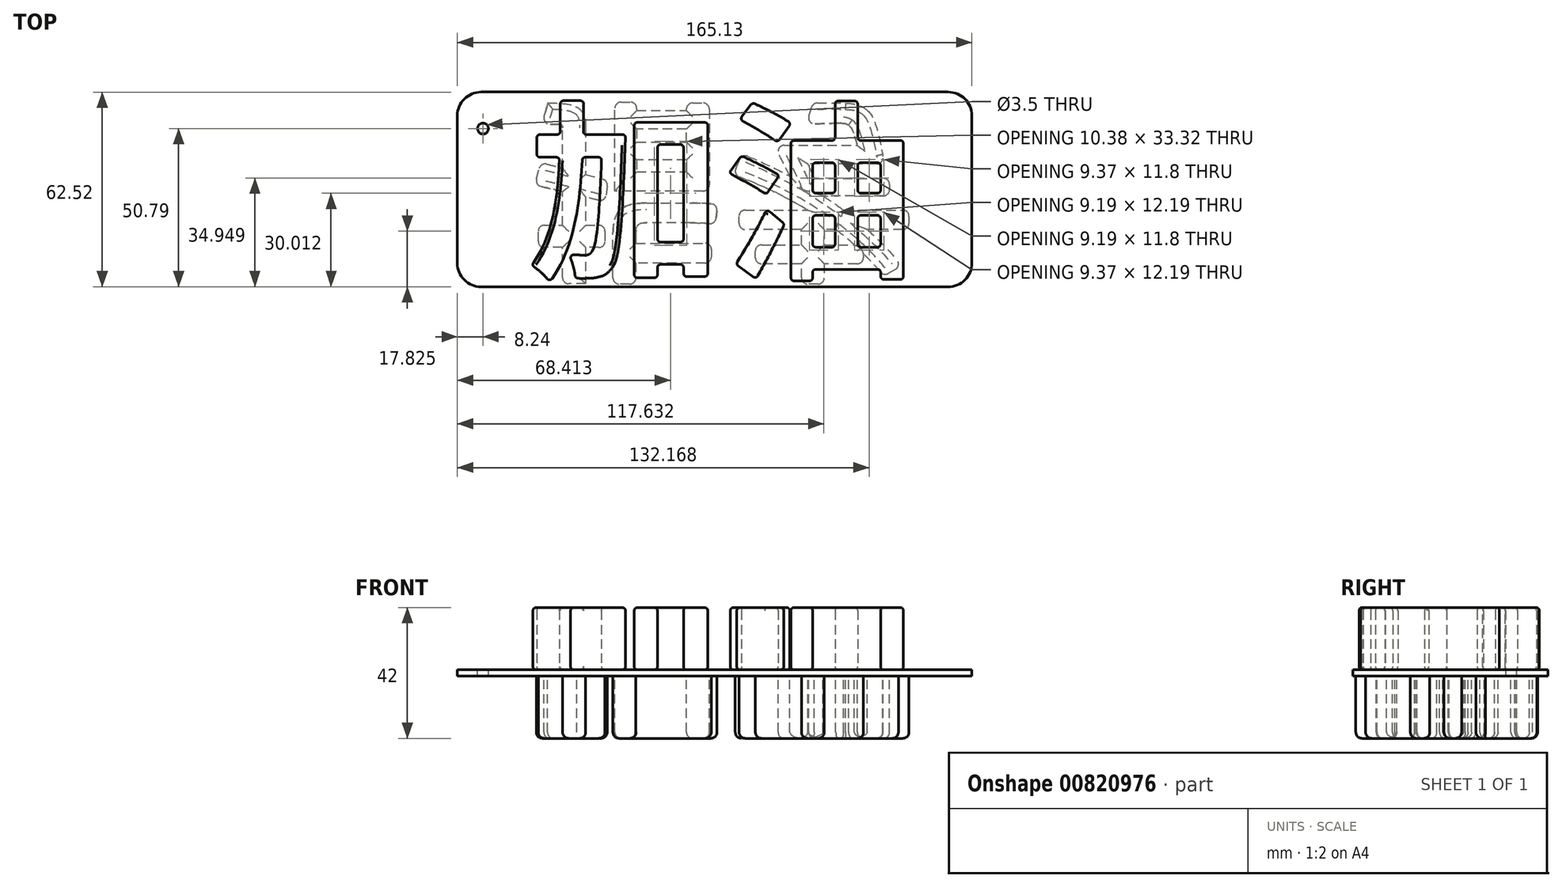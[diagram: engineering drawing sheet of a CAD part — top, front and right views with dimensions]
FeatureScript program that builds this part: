
annotation { "Feature Type Name" : "Feature", "Feature Type Description" : "" }
export const myFeature = defineFeature(function(context is Context, id is Id, definition is map)
    precondition{}
    {
        {
            var Q0;
            Q0=qCreatedBy(makeId("Top.planeOp"),FACE);
            var sketch = newSketch(context, id + "F0", { "sketchPlane" : qUnion([Q0])});
            skText(sketch, "E0", { "text": "加油", "fontName": "NotoSansCJKtc-Bold.otf"});
            const initialGuessF0  = {"E0": [-0.06597, -0.02194, 1, 0, 0.045]};
            skSetInitialGuess(sketch, initialGuessF0);
            skSolve(sketch);
        }
        {
            var Q0;
            Q0 = qSketchRegion(id + "F0", true);
            extrude(context, id + "F1", {"entities" : qUnion([Q0]), "depth" : 20 * mm, "offsetDistance" : 25.4 * mm});
        }
        {
            var Q0;
            Q0=makeQuery(id+"F1.opExtrude","CAP_EDGE",EDGE,{"disambiguationData":[OSD([sQuery(id+"F0.wireOp",EDGE,"E0.sketch_text.stroke-3")])],"isStart":false});
            var Q1;
            Q1=makeQuery(id+"F1.opExtrude","CAP_EDGE",EDGE,{"disambiguationData":[OSD([sQuery(id+"F0.wireOp",EDGE,"E0.sketch_text.stroke-35")])],"isStart":false});
            var Q2;
            Q2=makeQuery(id+"F1.opExtrude","CAP_EDGE",EDGE,{"disambiguationData":[OSD([sQuery(id+"F0.wireOp",EDGE,"E0.sketch_text.stroke-36")])],"isStart":false});
            var Q3;
            Q3=makeQuery(id+"F1.opExtrude","CAP_EDGE",EDGE,{"disambiguationData":[OSD([sQuery(id+"F0.wireOp",EDGE,"E0.sketch_text.stroke-37")])],"isStart":true});
            var Q4;
            Q4=makeQuery(id+"F1.opExtrude","CAP_EDGE",EDGE,{"disambiguationData":[OSD([sQuery(id+"F0.wireOp",EDGE,"E0.sketch_text.stroke-37")])],"isStart":false});
            var Q5;
            Q5=makeQuery(id+"F1.opExtrude","SWEPT_EDGE",EDGE,{"disambiguationData":[OSD([sQuery(id+"F0.wireOp",EDGE,"E0.sketch_text.stroke-31"),sQuery(id+"F0.wireOp",EDGE,"E0.sketch_text.stroke-34")])]});
            var Q6;
            Q6=makeQuery(id+"F1.opExtrude","CAP_EDGE",EDGE,{"disambiguationData":[OSD([sQuery(id+"F0.wireOp",EDGE,"E0.sketch_text.stroke-33")])],"isStart":false});
            var Q7;
            Q7=makeQuery(id+"F1.opExtrude","CAP_EDGE",EDGE,{"disambiguationData":[OSD([sQuery(id+"F0.wireOp",EDGE,"E0.sketch_text.stroke-34")])],"isStart":true});
            var Q8;
            Q8=makeQuery(id+"F1.opExtrude","CAP_EDGE",EDGE,{"disambiguationData":[OSD([sQuery(id+"F0.wireOp",EDGE,"E0.sketch_text.stroke-34")])],"isStart":false});
            var Q9;
            Q9=makeQuery(id+"F1.opExtrude","CAP_EDGE",EDGE,{"disambiguationData":[OSD([sQuery(id+"F0.wireOp",EDGE,"E0.sketch_text.stroke-39")])],"isStart":true});
            var Q10;
            Q10=makeQuery(id+"F1.opExtrude","CAP_EDGE",EDGE,{"disambiguationData":[OSD([sQuery(id+"F0.wireOp",EDGE,"E0.sketch_text.stroke-39")])],"isStart":false});
            var Q11;
            Q11=makeQuery(id+"F1.opExtrude","CAP_EDGE",EDGE,{"disambiguationData":[OSD([sQuery(id+"F0.wireOp",EDGE,"E0.sketch_text.stroke-40")])],"isStart":false});
            var Q12;
            Q12=makeQuery(id+"F1.opExtrude","CAP_EDGE",EDGE,{"disambiguationData":[OSD([sQuery(id+"F0.wireOp",EDGE,"E0.sketch_text.stroke-41")])],"isStart":false});
            var Q13;
            Q13=makeQuery(id+"F1.opExtrude","CAP_EDGE",EDGE,{"disambiguationData":[OSD([sQuery(id+"F0.wireOp",EDGE,"E0.sketch_text.stroke-42")])],"isStart":true});
            var Q14;
            Q14=makeQuery(id+"F1.opExtrude","CAP_EDGE",EDGE,{"disambiguationData":[OSD([sQuery(id+"F0.wireOp",EDGE,"E0.sketch_text.stroke-42")])],"isStart":false});
            var Q15;
            Q15=makeQuery(id+"F1.opExtrude","SWEPT_EDGE",EDGE,{"disambiguationData":[OSD([sQuery(id+"F0.wireOp",EDGE,"E0.sketch_text.stroke-0"),sQuery(id+"F0.wireOp",EDGE,"E0.sketch_text.stroke-18")])]});
            var Q16;
            Q16=makeQuery(id+"F1.opExtrude","SWEPT_EDGE",EDGE,{"disambiguationData":[OSD([sQuery(id+"F0.wireOp",EDGE,"E0.sketch_text.stroke-2"),sQuery(id+"F0.wireOp",EDGE,"E0.sketch_text.stroke-3")])]});
            var Q17;
            Q17=makeQuery(id+"F1.opExtrude","SWEPT_EDGE",EDGE,{"disambiguationData":[OSD([sQuery(id+"F0.wireOp",EDGE,"E0.sketch_text.stroke-4"),sQuery(id+"F0.wireOp",EDGE,"E0.sketch_text.stroke-5")])]});
            var Q18;
            Q18=makeQuery(id+"F1.opExtrude","CAP_EDGE",EDGE,{"disambiguationData":[OSD([sQuery(id+"F0.wireOp",EDGE,"E0.sketch_text.stroke-11")])],"isStart":false});
            var Q19;
            Q19=makeQuery(id+"F1.opExtrude","CAP_EDGE",EDGE,{"disambiguationData":[OSD([sQuery(id+"F0.wireOp",EDGE,"E0.sketch_text.stroke-12")])],"isStart":false});
            var Q20;
            Q20=makeQuery(id+"F1.opExtrude","CAP_EDGE",EDGE,{"disambiguationData":[OSD([sQuery(id+"F0.wireOp",EDGE,"E0.sketch_text.stroke-13")])],"isStart":true});
            var Q21;
            Q21=makeQuery(id+"F1.opExtrude","CAP_EDGE",EDGE,{"disambiguationData":[OSD([sQuery(id+"F0.wireOp",EDGE,"E0.sketch_text.stroke-13")])],"isStart":false});
            var Q22;
            Q22=makeQuery(id+"F1.opExtrude","CAP_EDGE",EDGE,{"disambiguationData":[OSD([sQuery(id+"F0.wireOp",EDGE,"E0.sketch_text.stroke-6")])],"isStart":true});
            var Q23;
            Q23=makeQuery(id+"F1.opExtrude","CAP_EDGE",EDGE,{"disambiguationData":[OSD([sQuery(id+"F0.wireOp",EDGE,"E0.sketch_text.stroke-14")])],"isStart":true});
            var Q24;
            Q24=makeQuery(id+"F1.opExtrude","CAP_EDGE",EDGE,{"disambiguationData":[OSD([sQuery(id+"F0.wireOp",EDGE,"E0.sketch_text.stroke-6")])],"isStart":false});
            var Q25;
            Q25=makeQuery(id+"F1.opExtrude","CAP_EDGE",EDGE,{"disambiguationData":[OSD([sQuery(id+"F0.wireOp",EDGE,"E0.sketch_text.stroke-14")])],"isStart":false});
            var Q26;
            Q26=makeQuery(id+"F1.opExtrude","CAP_EDGE",EDGE,{"disambiguationData":[OSD([sQuery(id+"F0.wireOp",EDGE,"E0.sketch_text.stroke-7")])],"isStart":true});
            var Q27;
            Q27=makeQuery(id+"F1.opExtrude","CAP_EDGE",EDGE,{"disambiguationData":[OSD([sQuery(id+"F0.wireOp",EDGE,"E0.sketch_text.stroke-15")])],"isStart":true});
            var Q28;
            Q28=makeQuery(id+"F1.opExtrude","CAP_EDGE",EDGE,{"disambiguationData":[OSD([sQuery(id+"F0.wireOp",EDGE,"E0.sketch_text.stroke-7")])],"isStart":false});
            var Q29;
            Q29=makeQuery(id+"F1.opExtrude","CAP_EDGE",EDGE,{"disambiguationData":[OSD([sQuery(id+"F0.wireOp",EDGE,"E0.sketch_text.stroke-15")])],"isStart":false});
            var Q30;
            Q30=makeQuery(id+"F1.opExtrude","CAP_EDGE",EDGE,{"disambiguationData":[OSD([sQuery(id+"F0.wireOp",EDGE,"E0.sketch_text.stroke-8")])],"isStart":true});
            var Q31;
            Q31=makeQuery(id+"F1.opExtrude","CAP_EDGE",EDGE,{"disambiguationData":[OSD([sQuery(id+"F0.wireOp",EDGE,"E0.sketch_text.stroke-16")])],"isStart":true});
            var Q32;
            Q32=makeQuery(id+"F1.opExtrude","CAP_EDGE",EDGE,{"disambiguationData":[OSD([sQuery(id+"F0.wireOp",EDGE,"E0.sketch_text.stroke-8")])],"isStart":false});
            var Q33;
            Q33=makeQuery(id+"F1.opExtrude","CAP_EDGE",EDGE,{"disambiguationData":[OSD([sQuery(id+"F0.wireOp",EDGE,"E0.sketch_text.stroke-16")])],"isStart":false});
            var Q34;
            Q34=makeQuery(id+"F1.opExtrude","CAP_EDGE",EDGE,{"disambiguationData":[OSD([sQuery(id+"F0.wireOp",EDGE,"E0.sketch_text.stroke-17")])],"isStart":false});
            var Q35;
            Q35=makeQuery(id+"F1.opExtrude","CAP_EDGE",EDGE,{"disambiguationData":[OSD([sQuery(id+"F0.wireOp",EDGE,"E0.sketch_text.stroke-10")])],"isStart":false});
            var Q36;
            Q36=makeQuery(id+"F1.opExtrude","SWEPT_EDGE",EDGE,{"disambiguationData":[OSD([sQuery(id+"F0.wireOp",EDGE,"E0.sketch_text.stroke-28"),sQuery(id+"F0.wireOp",EDGE,"E0.sketch_text.stroke-29")])]});
            var Q37;
            Q37=makeQuery(id+"F1.opExtrude","SWEPT_EDGE",EDGE,{"disambiguationData":[OSD([sQuery(id+"F0.wireOp",EDGE,"E0.sketch_text.stroke-23"),sQuery(id+"F0.wireOp",EDGE,"E0.sketch_text.stroke-24")])]});
            var Q38;
            Q38=makeQuery(id+"F1.opExtrude","SWEPT_EDGE",EDGE,{"disambiguationData":[OSD([sQuery(id+"F0.wireOp",EDGE,"E0.sketch_text.stroke-24"),sQuery(id+"F0.wireOp",EDGE,"E0.sketch_text.stroke-25")])]});
            var Q39;
            Q39=makeQuery(id+"F1.opExtrude","SWEPT_EDGE",EDGE,{"disambiguationData":[OSD([sQuery(id+"F0.wireOp",EDGE,"E0.sketch_text.stroke-27"),sQuery(id+"F0.wireOp",EDGE,"E0.sketch_text.stroke-28")])]});
            var Q40;
            Q40=makeQuery(id+"F1.opExtrude","SWEPT_EDGE",EDGE,{"disambiguationData":[OSD([sQuery(id+"F0.wireOp",EDGE,"E0.sketch_text.stroke-45"),sQuery(id+"F0.wireOp",EDGE,"E0.sketch_text.stroke-46")])]});
            var Q41;
            Q41=makeQuery(id+"F1.opExtrude","SWEPT_EDGE",EDGE,{"disambiguationData":[OSD([sQuery(id+"F0.wireOp",EDGE,"E0.sketch_text.stroke-61"),sQuery(id+"F0.wireOp",EDGE,"E0.sketch_text.stroke-62")])]});
            var Q42;
            Q42=makeQuery(id+"F1.opExtrude","SWEPT_EDGE",EDGE,{"disambiguationData":[OSD([sQuery(id+"F0.wireOp",EDGE,"E0.sketch_text.stroke-63"),sQuery(id+"F0.wireOp",EDGE,"E0.sketch_text.stroke-64")])]});
            var Q43;
            Q43=makeQuery(id+"F1.opExtrude","SWEPT_EDGE",EDGE,{"disambiguationData":[OSD([sQuery(id+"F0.wireOp",EDGE,"E0.sketch_text.stroke-48"),sQuery(id+"F0.wireOp",EDGE,"E0.sketch_text.stroke-49")])]});
            var Q44;
            Q44=makeQuery(id+"F1.opExtrude","SWEPT_EDGE",EDGE,{"disambiguationData":[OSD([sQuery(id+"F0.wireOp",EDGE,"E0.sketch_text.stroke-64"),sQuery(id+"F0.wireOp",EDGE,"E0.sketch_text.stroke-65")])]});
            var Q45;
            Q45=makeQuery(id+"F1.opExtrude","SWEPT_EDGE",EDGE,{"disambiguationData":[OSD([sQuery(id+"F0.wireOp",EDGE,"E0.sketch_text.stroke-49"),sQuery(id+"F0.wireOp",EDGE,"E0.sketch_text.stroke-50")])]});
            var Q46;
            Q46=makeQuery(id+"F1.opExtrude","SWEPT_EDGE",EDGE,{"disambiguationData":[OSD([sQuery(id+"F0.wireOp",EDGE,"E0.sketch_text.stroke-51"),sQuery(id+"F0.wireOp",EDGE,"E0.sketch_text.stroke-52")])]});
            var Q47;
            Q47=makeQuery(id+"F1.opExtrude","SWEPT_EDGE",EDGE,{"disambiguationData":[OSD([sQuery(id+"F0.wireOp",EDGE,"E0.sketch_text.stroke-67"),sQuery(id+"F0.wireOp",EDGE,"E0.sketch_text.stroke-68")])]});
            var Q48;
            Q48=makeQuery(id+"F1.opExtrude","SWEPT_EDGE",EDGE,{"disambiguationData":[OSD([sQuery(id+"F0.wireOp",EDGE,"E0.sketch_text.stroke-52"),sQuery(id+"F0.wireOp",EDGE,"E0.sketch_text.stroke-53")])]});
            var Q49;
            Q49=makeQuery(id+"F1.opExtrude","SWEPT_EDGE",EDGE,{"disambiguationData":[OSD([sQuery(id+"F0.wireOp",EDGE,"E0.sketch_text.stroke-68"),sQuery(id+"F0.wireOp",EDGE,"E0.sketch_text.stroke-69")])]});
            var Q50;
            Q50=makeQuery(id+"F1.opExtrude","SWEPT_EDGE",EDGE,{"disambiguationData":[OSD([sQuery(id+"F0.wireOp",EDGE,"E0.sketch_text.stroke-55"),sQuery(id+"F0.wireOp",EDGE,"E0.sketch_text.stroke-56")])]});
            var Q51;
            Q51=makeQuery(id+"F1.opExtrude","SWEPT_EDGE",EDGE,{"disambiguationData":[OSD([sQuery(id+"F0.wireOp",EDGE,"E0.sketch_text.stroke-56"),sQuery(id+"F0.wireOp",EDGE,"E0.sketch_text.stroke-57")])]});
            var Q52;
            Q52=makeQuery(id+"F1.opExtrude","SWEPT_EDGE",EDGE,{"disambiguationData":[OSD([sQuery(id+"F0.wireOp",EDGE,"E0.sketch_text.stroke-43"),sQuery(id+"F0.wireOp",EDGE,"E0.sketch_text.stroke-46")])]});
            var Q53;
            Q53=makeQuery(id+"F1.opExtrude","SWEPT_EDGE",EDGE,{"disambiguationData":[OSD([sQuery(id+"F0.wireOp",EDGE,"E0.sketch_text.stroke-59"),sQuery(id+"F0.wireOp",EDGE,"E0.sketch_text.stroke-70")])]});
            var Q54;
            Q54=makeQuery(id+"F1.opExtrude","CAP_EDGE",EDGE,{"disambiguationData":[OSD([sQuery(id+"F0.wireOp",EDGE,"E0.sketch_text.stroke-35")])],"isStart":true});
            var Q55;
            Q55=makeQuery(id+"F1.opExtrude","CAP_EDGE",EDGE,{"disambiguationData":[OSD([sQuery(id+"F0.wireOp",EDGE,"E0.sketch_text.stroke-36")])],"isStart":true});
            var Q56;
            Q56=makeQuery(id+"F1.opExtrude","SWEPT_EDGE",EDGE,{"disambiguationData":[OSD([sQuery(id+"F0.wireOp",EDGE,"E0.sketch_text.stroke-35"),sQuery(id+"F0.wireOp",EDGE,"E0.sketch_text.stroke-38")])]});
            var Q57;
            Q57=makeQuery(id+"F1.opExtrude","SWEPT_EDGE",EDGE,{"disambiguationData":[OSD([sQuery(id+"F0.wireOp",EDGE,"E0.sketch_text.stroke-35"),sQuery(id+"F0.wireOp",EDGE,"E0.sketch_text.stroke-36")])]});
            var Q58;
            Q58=makeQuery(id+"F1.opExtrude","CAP_EDGE",EDGE,{"disambiguationData":[OSD([sQuery(id+"F0.wireOp",EDGE,"E0.sketch_text.stroke-38")])],"isStart":false});
            var Q59;
            Q59=makeQuery(id+"F1.opExtrude","SWEPT_EDGE",EDGE,{"disambiguationData":[OSD([sQuery(id+"F0.wireOp",EDGE,"E0.sketch_text.stroke-36"),sQuery(id+"F0.wireOp",EDGE,"E0.sketch_text.stroke-37")])]});
            var Q60;
            Q60=makeQuery(id+"F1.opExtrude","SWEPT_EDGE",EDGE,{"disambiguationData":[OSD([sQuery(id+"F0.wireOp",EDGE,"E0.sketch_text.stroke-37"),sQuery(id+"F0.wireOp",EDGE,"E0.sketch_text.stroke-38")])]});
            var Q61;
            Q61=makeQuery(id+"F1.opExtrude","SWEPT_EDGE",EDGE,{"disambiguationData":[OSD([sQuery(id+"F0.wireOp",EDGE,"E0.sketch_text.stroke-32"),sQuery(id+"F0.wireOp",EDGE,"E0.sketch_text.stroke-33")])]});
            var Q62;
            Q62=makeQuery(id+"F1.opExtrude","SWEPT_EDGE",EDGE,{"disambiguationData":[OSD([sQuery(id+"F0.wireOp",EDGE,"E0.sketch_text.stroke-33"),sQuery(id+"F0.wireOp",EDGE,"E0.sketch_text.stroke-34")])]});
            var Q63;
            Q63=makeQuery(id+"F1.opExtrude","CAP_EDGE",EDGE,{"disambiguationData":[OSD([sQuery(id+"F0.wireOp",EDGE,"E0.sketch_text.stroke-31")])],"isStart":true});
            var Q64;
            Q64=makeQuery(id+"F1.opExtrude","CAP_EDGE",EDGE,{"disambiguationData":[OSD([sQuery(id+"F0.wireOp",EDGE,"E0.sketch_text.stroke-32")])],"isStart":true});
            var Q65;
            Q65=makeQuery(id+"F1.opExtrude","CAP_EDGE",EDGE,{"disambiguationData":[OSD([sQuery(id+"F0.wireOp",EDGE,"E0.sketch_text.stroke-33")])],"isStart":true});
            var Q66;
            Q66=makeQuery(id+"F1.opExtrude","SWEPT_EDGE",EDGE,{"disambiguationData":[OSD([sQuery(id+"F0.wireOp",EDGE,"E0.sketch_text.stroke-39"),sQuery(id+"F0.wireOp",EDGE,"E0.sketch_text.stroke-42")])]});
            var Q67;
            Q67=makeQuery(id+"F1.opExtrude","CAP_EDGE",EDGE,{"disambiguationData":[OSD([sQuery(id+"F0.wireOp",EDGE,"E0.sketch_text.stroke-40")])],"isStart":true});
            var Q68;
            Q68=makeQuery(id+"F1.opExtrude","SWEPT_EDGE",EDGE,{"disambiguationData":[OSD([sQuery(id+"F0.wireOp",EDGE,"E0.sketch_text.stroke-39"),sQuery(id+"F0.wireOp",EDGE,"E0.sketch_text.stroke-40")])]});
            var Q69;
            Q69=makeQuery(id+"F1.opExtrude","SWEPT_EDGE",EDGE,{"disambiguationData":[OSD([sQuery(id+"F0.wireOp",EDGE,"E0.sketch_text.stroke-40"),sQuery(id+"F0.wireOp",EDGE,"E0.sketch_text.stroke-41")])]});
            var Q70;
            Q70=makeQuery(id+"F1.opExtrude","CAP_EDGE",EDGE,{"disambiguationData":[OSD([sQuery(id+"F0.wireOp",EDGE,"E0.sketch_text.stroke-41")])],"isStart":true});
            var Q71;
            Q71=makeQuery(id+"F1.opExtrude","SWEPT_EDGE",EDGE,{"disambiguationData":[OSD([sQuery(id+"F0.wireOp",EDGE,"E0.sketch_text.stroke-41"),sQuery(id+"F0.wireOp",EDGE,"E0.sketch_text.stroke-42")])]});
            var Q72;
            Q72=makeQuery(id+"F1.opExtrude","SWEPT_EDGE",EDGE,{"disambiguationData":[OSD([sQuery(id+"F0.wireOp",EDGE,"E0.sketch_text.stroke-12"),sQuery(id+"F0.wireOp",EDGE,"E0.sketch_text.stroke-13")])]});
            var Q73;
            Q73=makeQuery(id+"F1.opExtrude","SWEPT_EDGE",EDGE,{"disambiguationData":[OSD([sQuery(id+"F0.wireOp",EDGE,"E0.sketch_text.stroke-13"),sQuery(id+"F0.wireOp",EDGE,"E0.sketch_text.stroke-14")])]});
            var Q74;
            Q74=makeQuery(id+"F1.opExtrude","SWEPT_EDGE",EDGE,{"disambiguationData":[OSD([sQuery(id+"F0.wireOp",EDGE,"E0.sketch_text.stroke-14"),sQuery(id+"F0.wireOp",EDGE,"E0.sketch_text.stroke-15")])]});
            var Q75;
            Q75=makeQuery(id+"F1.opExtrude","SWEPT_EDGE",EDGE,{"disambiguationData":[OSD([sQuery(id+"F0.wireOp",EDGE,"E0.sketch_text.stroke-3"),sQuery(id+"F0.wireOp",EDGE,"E0.sketch_text.stroke-4")])]});
            var Q76;
            Q76=makeQuery(id+"F1.opExtrude","SWEPT_EDGE",EDGE,{"disambiguationData":[OSD([sQuery(id+"F0.wireOp",EDGE,"E0.sketch_text.stroke-5"),sQuery(id+"F0.wireOp",EDGE,"E0.sketch_text.stroke-6")])]});
            var Q77;
            Q77=makeQuery(id+"F1.opExtrude","SWEPT_EDGE",EDGE,{"disambiguationData":[OSD([sQuery(id+"F0.wireOp",EDGE,"E0.sketch_text.stroke-6"),sQuery(id+"F0.wireOp",EDGE,"E0.sketch_text.stroke-7")])]});
            var Q78;
            Q78=makeQuery(id+"F1.opExtrude","SWEPT_EDGE",EDGE,{"disambiguationData":[OSD([sQuery(id+"F0.wireOp",EDGE,"E0.sketch_text.stroke-7"),sQuery(id+"F0.wireOp",EDGE,"E0.sketch_text.stroke-8")])]});
            var Q79;
            Q79=makeQuery(id+"F1.opExtrude","SWEPT_EDGE",EDGE,{"disambiguationData":[OSD([sQuery(id+"F0.wireOp",EDGE,"E0.sketch_text.stroke-8"),sQuery(id+"F0.wireOp",EDGE,"E0.sketch_text.stroke-9")])]});
            var Q80;
            Q80=makeQuery(id+"F1.opExtrude","SWEPT_EDGE",EDGE,{"disambiguationData":[OSD([sQuery(id+"F0.wireOp",EDGE,"E0.sketch_text.stroke-9"),sQuery(id+"F0.wireOp",EDGE,"E0.sketch_text.stroke-10")])]});
            var Q81;
            Q81=makeQuery(id+"F1.opExtrude","SWEPT_EDGE",EDGE,{"disambiguationData":[OSD([sQuery(id+"F0.wireOp",EDGE,"E0.sketch_text.stroke-10"),sQuery(id+"F0.wireOp",EDGE,"E0.sketch_text.stroke-11")])]});
            var Q82;
            Q82=makeQuery(id+"F1.opExtrude","SWEPT_EDGE",EDGE,{"disambiguationData":[OSD([sQuery(id+"F0.wireOp",EDGE,"E0.sketch_text.stroke-11"),sQuery(id+"F0.wireOp",EDGE,"E0.sketch_text.stroke-12")])]});
            var Q83;
            Q83=makeQuery(id+"F1.opExtrude","CAP_EDGE",EDGE,{"disambiguationData":[OSD([sQuery(id+"F0.wireOp",EDGE,"E0.sketch_text.stroke-3")])],"isStart":true});
            var Q84;
            Q84=makeQuery(id+"F1.opExtrude","CAP_EDGE",EDGE,{"disambiguationData":[OSD([sQuery(id+"F0.wireOp",EDGE,"E0.sketch_text.stroke-11")])],"isStart":true});
            var Q85;
            Q85=makeQuery(id+"F1.opExtrude","CAP_EDGE",EDGE,{"disambiguationData":[OSD([sQuery(id+"F0.wireOp",EDGE,"E0.sketch_text.stroke-4")])],"isStart":true});
            var Q86;
            Q86=makeQuery(id+"F1.opExtrude","CAP_EDGE",EDGE,{"disambiguationData":[OSD([sQuery(id+"F0.wireOp",EDGE,"E0.sketch_text.stroke-12")])],"isStart":true});
            var Q87;
            Q87=makeQuery(id+"F1.opExtrude","SWEPT_EDGE",EDGE,{"disambiguationData":[OSD([sQuery(id+"F0.wireOp",EDGE,"E0.sketch_text.stroke-15"),sQuery(id+"F0.wireOp",EDGE,"E0.sketch_text.stroke-16")])]});
            var Q88;
            Q88=makeQuery(id+"F1.opExtrude","CAP_EDGE",EDGE,{"disambiguationData":[OSD([sQuery(id+"F0.wireOp",EDGE,"E0.sketch_text.stroke-4")])],"isStart":false});
            var Q89;
            Q89=makeQuery(id+"F1.opExtrude","SWEPT_EDGE",EDGE,{"disambiguationData":[OSD([sQuery(id+"F0.wireOp",EDGE,"E0.sketch_text.stroke-16"),sQuery(id+"F0.wireOp",EDGE,"E0.sketch_text.stroke-17")])]});
            var Q90;
            Q90=makeQuery(id+"F1.opExtrude","CAP_EDGE",EDGE,{"disambiguationData":[OSD([sQuery(id+"F0.wireOp",EDGE,"E0.sketch_text.stroke-5")])],"isStart":true});
            var Q91;
            Q91=makeQuery(id+"F1.opExtrude","SWEPT_EDGE",EDGE,{"disambiguationData":[OSD([sQuery(id+"F0.wireOp",EDGE,"E0.sketch_text.stroke-17"),sQuery(id+"F0.wireOp",EDGE,"E0.sketch_text.stroke-18")])]});
            var Q92;
            Q92=makeQuery(id+"F1.opExtrude","CAP_EDGE",EDGE,{"disambiguationData":[OSD([sQuery(id+"F0.wireOp",EDGE,"E0.sketch_text.stroke-5")])],"isStart":false});
            var Q93;
            Q93=makeQuery(id+"F1.opExtrude","CAP_EDGE",EDGE,{"disambiguationData":[OSD([sQuery(id+"F0.wireOp",EDGE,"E0.sketch_text.stroke-0")])],"isStart":true});
            var Q94;
            Q94=makeQuery(id+"F1.opExtrude","CAP_EDGE",EDGE,{"disambiguationData":[OSD([sQuery(id+"F0.wireOp",EDGE,"E0.sketch_text.stroke-1")])],"isStart":true});
            var Q95;
            Q95=makeQuery(id+"F1.opExtrude","CAP_EDGE",EDGE,{"disambiguationData":[OSD([sQuery(id+"F0.wireOp",EDGE,"E0.sketch_text.stroke-9")])],"isStart":true});
            var Q96;
            Q96=makeQuery(id+"F1.opExtrude","CAP_EDGE",EDGE,{"disambiguationData":[OSD([sQuery(id+"F0.wireOp",EDGE,"E0.sketch_text.stroke-9")])],"isStart":false});
            var Q97;
            Q97=makeQuery(id+"F1.opExtrude","CAP_EDGE",EDGE,{"disambiguationData":[OSD([sQuery(id+"F0.wireOp",EDGE,"E0.sketch_text.stroke-2")])],"isStart":true});
            var Q98;
            Q98=makeQuery(id+"F1.opExtrude","CAP_EDGE",EDGE,{"disambiguationData":[OSD([sQuery(id+"F0.wireOp",EDGE,"E0.sketch_text.stroke-10")])],"isStart":true});
            var Q99;
            Q99=makeQuery(id+"F1.opExtrude","CAP_EDGE",EDGE,{"disambiguationData":[OSD([sQuery(id+"F0.wireOp",EDGE,"E0.sketch_text.stroke-18")])],"isStart":true});
            var Q100;
            Q100=makeQuery(id+"F1.opExtrude","CAP_EDGE",EDGE,{"disambiguationData":[OSD([sQuery(id+"F0.wireOp",EDGE,"E0.sketch_text.stroke-18")])],"isStart":false});
            var Q101;
            Q101=makeQuery(id+"F1.opExtrude","CAP_EDGE",EDGE,{"disambiguationData":[OSD([sQuery(id+"F0.wireOp",EDGE,"E0.sketch_text.stroke-27")])],"isStart":true});
            var Q102;
            Q102=makeQuery(id+"F1.opExtrude","SWEPT_EDGE",EDGE,{"disambiguationData":[OSD([sQuery(id+"F0.wireOp",EDGE,"E0.sketch_text.stroke-29"),sQuery(id+"F0.wireOp",EDGE,"E0.sketch_text.stroke-30")])]});
            var Q103;
            Q103=makeQuery(id+"F1.opExtrude","CAP_EDGE",EDGE,{"disambiguationData":[OSD([sQuery(id+"F0.wireOp",EDGE,"E0.sketch_text.stroke-19")])],"isStart":false});
            var Q104;
            Q104=makeQuery(id+"F1.opExtrude","CAP_EDGE",EDGE,{"disambiguationData":[OSD([sQuery(id+"F0.wireOp",EDGE,"E0.sketch_text.stroke-27")])],"isStart":false});
            var Q105;
            Q105=makeQuery(id+"F1.opExtrude","CAP_EDGE",EDGE,{"disambiguationData":[OSD([sQuery(id+"F0.wireOp",EDGE,"E0.sketch_text.stroke-20")])],"isStart":true});
            var Q106;
            Q106=makeQuery(id+"F1.opExtrude","CAP_EDGE",EDGE,{"disambiguationData":[OSD([sQuery(id+"F0.wireOp",EDGE,"E0.sketch_text.stroke-28")])],"isStart":true});
            var Q107;
            Q107=makeQuery(id+"F1.opExtrude","CAP_EDGE",EDGE,{"disambiguationData":[OSD([sQuery(id+"F0.wireOp",EDGE,"E0.sketch_text.stroke-20")])],"isStart":false});
            var Q108;
            Q108=makeQuery(id+"F1.opExtrude","CAP_EDGE",EDGE,{"disambiguationData":[OSD([sQuery(id+"F0.wireOp",EDGE,"E0.sketch_text.stroke-28")])],"isStart":false});
            var Q109;
            Q109=makeQuery(id+"F1.opExtrude","CAP_EDGE",EDGE,{"disambiguationData":[OSD([sQuery(id+"F0.wireOp",EDGE,"E0.sketch_text.stroke-29")])],"isStart":true});
            var Q110;
            Q110=makeQuery(id+"F1.opExtrude","CAP_EDGE",EDGE,{"disambiguationData":[OSD([sQuery(id+"F0.wireOp",EDGE,"E0.sketch_text.stroke-21")])],"isStart":false});
            var Q111;
            Q111=makeQuery(id+"F1.opExtrude","CAP_EDGE",EDGE,{"disambiguationData":[OSD([sQuery(id+"F0.wireOp",EDGE,"E0.sketch_text.stroke-29")])],"isStart":false});
            var Q112;
            Q112=makeQuery(id+"F1.opExtrude","SWEPT_EDGE",EDGE,{"disambiguationData":[OSD([sQuery(id+"F0.wireOp",EDGE,"E0.sketch_text.stroke-19"),sQuery(id+"F0.wireOp",EDGE,"E0.sketch_text.stroke-22")])]});
            var Q113;
            Q113=makeQuery(id+"F1.opExtrude","CAP_EDGE",EDGE,{"disambiguationData":[OSD([sQuery(id+"F0.wireOp",EDGE,"E0.sketch_text.stroke-22")])],"isStart":true});
            var Q114;
            Q114=makeQuery(id+"F1.opExtrude","CAP_EDGE",EDGE,{"disambiguationData":[OSD([sQuery(id+"F0.wireOp",EDGE,"E0.sketch_text.stroke-30")])],"isStart":true});
            var Q115;
            Q115=makeQuery(id+"F1.opExtrude","CAP_EDGE",EDGE,{"disambiguationData":[OSD([sQuery(id+"F0.wireOp",EDGE,"E0.sketch_text.stroke-22")])],"isStart":false});
            var Q116;
            Q116=makeQuery(id+"F1.opExtrude","CAP_EDGE",EDGE,{"disambiguationData":[OSD([sQuery(id+"F0.wireOp",EDGE,"E0.sketch_text.stroke-30")])],"isStart":false});
            var Q117;
            Q117=makeQuery(id+"F1.opExtrude","CAP_EDGE",EDGE,{"disambiguationData":[OSD([sQuery(id+"F0.wireOp",EDGE,"E0.sketch_text.stroke-23")])],"isStart":true});
            var Q118;
            Q118=makeQuery(id+"F1.opExtrude","SWEPT_EDGE",EDGE,{"disambiguationData":[OSD([sQuery(id+"F0.wireOp",EDGE,"E0.sketch_text.stroke-21"),sQuery(id+"F0.wireOp",EDGE,"E0.sketch_text.stroke-22")])]});
            var Q119;
            Q119=makeQuery(id+"F1.opExtrude","CAP_EDGE",EDGE,{"disambiguationData":[OSD([sQuery(id+"F0.wireOp",EDGE,"E0.sketch_text.stroke-24")])],"isStart":true});
            var Q120;
            Q120=makeQuery(id+"F1.opExtrude","CAP_EDGE",EDGE,{"disambiguationData":[OSD([sQuery(id+"F0.wireOp",EDGE,"E0.sketch_text.stroke-24")])],"isStart":false});
            var Q121;
            Q121=makeQuery(id+"F1.opExtrude","CAP_EDGE",EDGE,{"disambiguationData":[OSD([sQuery(id+"F0.wireOp",EDGE,"E0.sketch_text.stroke-25")])],"isStart":true});
            var Q122;
            Q122=makeQuery(id+"F1.opExtrude","SWEPT_EDGE",EDGE,{"disambiguationData":[OSD([sQuery(id+"F0.wireOp",EDGE,"E0.sketch_text.stroke-25"),sQuery(id+"F0.wireOp",EDGE,"E0.sketch_text.stroke-26")])]});
            var Q123;
            Q123=makeQuery(id+"F1.opExtrude","CAP_EDGE",EDGE,{"disambiguationData":[OSD([sQuery(id+"F0.wireOp",EDGE,"E0.sketch_text.stroke-25")])],"isStart":false});
            var Q124;
            Q124=makeQuery(id+"F1.opExtrude","SWEPT_EDGE",EDGE,{"disambiguationData":[OSD([sQuery(id+"F0.wireOp",EDGE,"E0.sketch_text.stroke-26"),sQuery(id+"F0.wireOp",EDGE,"E0.sketch_text.stroke-27")])]});
            var Q125;
            Q125=makeQuery(id+"F1.opExtrude","CAP_EDGE",EDGE,{"disambiguationData":[OSD([sQuery(id+"F0.wireOp",EDGE,"E0.sketch_text.stroke-26")])],"isStart":true});
            var Q126;
            Q126=makeQuery(id+"F1.opExtrude","CAP_EDGE",EDGE,{"disambiguationData":[OSD([sQuery(id+"F0.wireOp",EDGE,"E0.sketch_text.stroke-26")])],"isStart":false});
            var Q127;
            Q127=makeQuery(id+"F1.opExtrude","CAP_EDGE",EDGE,{"disambiguationData":[OSD([sQuery(id+"F0.wireOp",EDGE,"E0.sketch_text.stroke-70")])],"isStart":false});
            var Q128;
            Q128=makeQuery(id+"F1.opExtrude","SWEPT_EDGE",EDGE,{"disambiguationData":[OSD([sQuery(id+"F0.wireOp",EDGE,"E0.sketch_text.stroke-44"),sQuery(id+"F0.wireOp",EDGE,"E0.sketch_text.stroke-45")])]});
            var Q129;
            Q129=makeQuery(id+"F1.opExtrude","CAP_EDGE",EDGE,{"disambiguationData":[OSD([sQuery(id+"F0.wireOp",EDGE,"E0.sketch_text.stroke-43")])],"isStart":true});
            var Q130;
            Q130=makeQuery(id+"F1.opExtrude","CAP_EDGE",EDGE,{"disambiguationData":[OSD([sQuery(id+"F0.wireOp",EDGE,"E0.sketch_text.stroke-51")])],"isStart":true});
            var Q131;
            Q131=makeQuery(id+"F1.opExtrude","CAP_EDGE",EDGE,{"disambiguationData":[OSD([sQuery(id+"F0.wireOp",EDGE,"E0.sketch_text.stroke-59")])],"isStart":true});
            var Q132;
            Q132=makeQuery(id+"F1.opExtrude","CAP_EDGE",EDGE,{"disambiguationData":[OSD([sQuery(id+"F0.wireOp",EDGE,"E0.sketch_text.stroke-67")])],"isStart":true});
            var Q133;
            Q133=makeQuery(id+"F1.opExtrude","CAP_EDGE",EDGE,{"disambiguationData":[OSD([sQuery(id+"F0.wireOp",EDGE,"E0.sketch_text.stroke-43")])],"isStart":false});
            var Q134;
            Q134=makeQuery(id+"F1.opExtrude","CAP_EDGE",EDGE,{"disambiguationData":[OSD([sQuery(id+"F0.wireOp",EDGE,"E0.sketch_text.stroke-51")])],"isStart":false});
            var Q135;
            Q135=makeQuery(id+"F1.opExtrude","CAP_EDGE",EDGE,{"disambiguationData":[OSD([sQuery(id+"F0.wireOp",EDGE,"E0.sketch_text.stroke-67")])],"isStart":false});
            var Q136;
            Q136=makeQuery(id+"F1.opExtrude","SWEPT_EDGE",EDGE,{"disambiguationData":[OSD([sQuery(id+"F0.wireOp",EDGE,"E0.sketch_text.stroke-62"),sQuery(id+"F0.wireOp",EDGE,"E0.sketch_text.stroke-63")])]});
            var Q137;
            Q137=makeQuery(id+"F1.opExtrude","CAP_EDGE",EDGE,{"disambiguationData":[OSD([sQuery(id+"F0.wireOp",EDGE,"E0.sketch_text.stroke-44")])],"isStart":true});
            var Q138;
            Q138=makeQuery(id+"F1.opExtrude","CAP_EDGE",EDGE,{"disambiguationData":[OSD([sQuery(id+"F0.wireOp",EDGE,"E0.sketch_text.stroke-52")])],"isStart":true});
            var Q139;
            Q139=makeQuery(id+"F1.opExtrude","CAP_EDGE",EDGE,{"disambiguationData":[OSD([sQuery(id+"F0.wireOp",EDGE,"E0.sketch_text.stroke-60")])],"isStart":true});
            var Q140;
            Q140=makeQuery(id+"F1.opExtrude","CAP_EDGE",EDGE,{"disambiguationData":[OSD([sQuery(id+"F0.wireOp",EDGE,"E0.sketch_text.stroke-68")])],"isStart":true});
            var Q141;
            Q141=makeQuery(id+"F1.opExtrude","CAP_EDGE",EDGE,{"disambiguationData":[OSD([sQuery(id+"F0.wireOp",EDGE,"E0.sketch_text.stroke-44")])],"isStart":false});
            var Q142;
            Q142=makeQuery(id+"F1.opExtrude","CAP_EDGE",EDGE,{"disambiguationData":[OSD([sQuery(id+"F0.wireOp",EDGE,"E0.sketch_text.stroke-52")])],"isStart":false});
            var Q143;
            Q143=makeQuery(id+"F1.opExtrude","CAP_EDGE",EDGE,{"disambiguationData":[OSD([sQuery(id+"F0.wireOp",EDGE,"E0.sketch_text.stroke-68")])],"isStart":false});
            var Q144;
            Q144=makeQuery(id+"F1.opExtrude","CAP_EDGE",EDGE,{"disambiguationData":[OSD([sQuery(id+"F0.wireOp",EDGE,"E0.sketch_text.stroke-45")])],"isStart":true});
            var Q145;
            Q145=makeQuery(id+"F1.opExtrude","CAP_EDGE",EDGE,{"disambiguationData":[OSD([sQuery(id+"F0.wireOp",EDGE,"E0.sketch_text.stroke-53")])],"isStart":true});
            var Q146;
            Q146=makeQuery(id+"F1.opExtrude","CAP_EDGE",EDGE,{"disambiguationData":[OSD([sQuery(id+"F0.wireOp",EDGE,"E0.sketch_text.stroke-61")])],"isStart":true});
            var Q147;
            Q147=makeQuery(id+"F1.opExtrude","CAP_EDGE",EDGE,{"disambiguationData":[OSD([sQuery(id+"F0.wireOp",EDGE,"E0.sketch_text.stroke-69")])],"isStart":true});
            var Q148;
            Q148=makeQuery(id+"F1.opExtrude","CAP_EDGE",EDGE,{"disambiguationData":[OSD([sQuery(id+"F0.wireOp",EDGE,"E0.sketch_text.stroke-45")])],"isStart":false});
            var Q149;
            Q149=makeQuery(id+"F1.opExtrude","SWEPT_EDGE",EDGE,{"disambiguationData":[OSD([sQuery(id+"F0.wireOp",EDGE,"E0.sketch_text.stroke-65"),sQuery(id+"F0.wireOp",EDGE,"E0.sketch_text.stroke-66")])]});
            var Q150;
            Q150=makeQuery(id+"F1.opExtrude","CAP_EDGE",EDGE,{"disambiguationData":[OSD([sQuery(id+"F0.wireOp",EDGE,"E0.sketch_text.stroke-53")])],"isStart":false});
            var Q151;
            Q151=makeQuery(id+"F1.opExtrude","CAP_EDGE",EDGE,{"disambiguationData":[OSD([sQuery(id+"F0.wireOp",EDGE,"E0.sketch_text.stroke-69")])],"isStart":false});
            var Q152;
            Q152=makeQuery(id+"F1.opExtrude","SWEPT_EDGE",EDGE,{"disambiguationData":[OSD([sQuery(id+"F0.wireOp",EDGE,"E0.sketch_text.stroke-51"),sQuery(id+"F0.wireOp",EDGE,"E0.sketch_text.stroke-54")])]});
            var Q153;
            Q153=makeQuery(id+"F1.opExtrude","SWEPT_EDGE",EDGE,{"disambiguationData":[OSD([sQuery(id+"F0.wireOp",EDGE,"E0.sketch_text.stroke-66"),sQuery(id+"F0.wireOp",EDGE,"E0.sketch_text.stroke-67")])]});
            var Q154;
            Q154=makeQuery(id+"F1.opExtrude","CAP_EDGE",EDGE,{"disambiguationData":[OSD([sQuery(id+"F0.wireOp",EDGE,"E0.sketch_text.stroke-46")])],"isStart":true});
            var Q155;
            Q155=makeQuery(id+"F1.opExtrude","CAP_EDGE",EDGE,{"disambiguationData":[OSD([sQuery(id+"F0.wireOp",EDGE,"E0.sketch_text.stroke-62")])],"isStart":true});
            var Q156;
            Q156=makeQuery(id+"F1.opExtrude","CAP_EDGE",EDGE,{"disambiguationData":[OSD([sQuery(id+"F0.wireOp",EDGE,"E0.sketch_text.stroke-54")])],"isStart":true});
            var Q157;
            Q157=makeQuery(id+"F1.opExtrude","CAP_EDGE",EDGE,{"disambiguationData":[OSD([sQuery(id+"F0.wireOp",EDGE,"E0.sketch_text.stroke-70")])],"isStart":true});
            var Q158;
            Q158=makeQuery(id+"F1.opExtrude","CAP_EDGE",EDGE,{"disambiguationData":[OSD([sQuery(id+"F0.wireOp",EDGE,"E0.sketch_text.stroke-46")])],"isStart":false});
            var Q159;
            Q159=makeQuery(id+"F1.opExtrude","CAP_EDGE",EDGE,{"disambiguationData":[OSD([sQuery(id+"F0.wireOp",EDGE,"E0.sketch_text.stroke-54")])],"isStart":false});
            var Q160;
            Q160=makeQuery(id+"F1.opExtrude","CAP_EDGE",EDGE,{"disambiguationData":[OSD([sQuery(id+"F0.wireOp",EDGE,"E0.sketch_text.stroke-62")])],"isStart":false});
            var Q161;
            Q161=makeQuery(id+"F1.opExtrude","CAP_EDGE",EDGE,{"disambiguationData":[OSD([sQuery(id+"F0.wireOp",EDGE,"E0.sketch_text.stroke-47")])],"isStart":true});
            var Q162;
            Q162=makeQuery(id+"F1.opExtrude","CAP_EDGE",EDGE,{"disambiguationData":[OSD([sQuery(id+"F0.wireOp",EDGE,"E0.sketch_text.stroke-55")])],"isStart":true});
            var Q163;
            Q163=makeQuery(id+"F1.opExtrude","CAP_EDGE",EDGE,{"disambiguationData":[OSD([sQuery(id+"F0.wireOp",EDGE,"E0.sketch_text.stroke-63")])],"isStart":true});
            var Q164;
            Q164=makeQuery(id+"F1.opExtrude","SWEPT_EDGE",EDGE,{"disambiguationData":[OSD([sQuery(id+"F0.wireOp",EDGE,"E0.sketch_text.stroke-53"),sQuery(id+"F0.wireOp",EDGE,"E0.sketch_text.stroke-54")])]});
            var Q165;
            Q165=makeQuery(id+"F1.opExtrude","CAP_EDGE",EDGE,{"disambiguationData":[OSD([sQuery(id+"F0.wireOp",EDGE,"E0.sketch_text.stroke-47")])],"isStart":false});
            var Q166;
            Q166=makeQuery(id+"F1.opExtrude","CAP_EDGE",EDGE,{"disambiguationData":[OSD([sQuery(id+"F0.wireOp",EDGE,"E0.sketch_text.stroke-55")])],"isStart":false});
            var Q167;
            Q167=makeQuery(id+"F1.opExtrude","CAP_EDGE",EDGE,{"disambiguationData":[OSD([sQuery(id+"F0.wireOp",EDGE,"E0.sketch_text.stroke-63")])],"isStart":false});
            var Q168;
            Q168=makeQuery(id+"F1.opExtrude","SWEPT_EDGE",EDGE,{"disambiguationData":[OSD([sQuery(id+"F0.wireOp",EDGE,"E0.sketch_text.stroke-55"),sQuery(id+"F0.wireOp",EDGE,"E0.sketch_text.stroke-58")])]});
            var Q169;
            Q169=makeQuery(id+"F1.opExtrude","CAP_EDGE",EDGE,{"disambiguationData":[OSD([sQuery(id+"F0.wireOp",EDGE,"E0.sketch_text.stroke-48")])],"isStart":true});
            var Q170;
            Q170=makeQuery(id+"F1.opExtrude","CAP_EDGE",EDGE,{"disambiguationData":[OSD([sQuery(id+"F0.wireOp",EDGE,"E0.sketch_text.stroke-56")])],"isStart":true});
            var Q171;
            Q171=makeQuery(id+"F1.opExtrude","CAP_EDGE",EDGE,{"disambiguationData":[OSD([sQuery(id+"F0.wireOp",EDGE,"E0.sketch_text.stroke-64")])],"isStart":true});
            var Q172;
            Q172=makeQuery(id+"F1.opExtrude","CAP_EDGE",EDGE,{"disambiguationData":[OSD([sQuery(id+"F0.wireOp",EDGE,"E0.sketch_text.stroke-48")])],"isStart":false});
            var Q173;
            Q173=makeQuery(id+"F1.opExtrude","CAP_EDGE",EDGE,{"disambiguationData":[OSD([sQuery(id+"F0.wireOp",EDGE,"E0.sketch_text.stroke-56")])],"isStart":false});
            var Q174;
            Q174=makeQuery(id+"F1.opExtrude","CAP_EDGE",EDGE,{"disambiguationData":[OSD([sQuery(id+"F0.wireOp",EDGE,"E0.sketch_text.stroke-64")])],"isStart":false});
            var Q175;
            Q175=makeQuery(id+"F1.opExtrude","CAP_EDGE",EDGE,{"disambiguationData":[OSD([sQuery(id+"F0.wireOp",EDGE,"E0.sketch_text.stroke-49")])],"isStart":true});
            var Q176;
            Q176=makeQuery(id+"F1.opExtrude","CAP_EDGE",EDGE,{"disambiguationData":[OSD([sQuery(id+"F0.wireOp",EDGE,"E0.sketch_text.stroke-57")])],"isStart":true});
            var Q177;
            Q177=makeQuery(id+"F1.opExtrude","CAP_EDGE",EDGE,{"disambiguationData":[OSD([sQuery(id+"F0.wireOp",EDGE,"E0.sketch_text.stroke-65")])],"isStart":true});
            var Q178;
            Q178=makeQuery(id+"F1.opExtrude","SWEPT_EDGE",EDGE,{"disambiguationData":[OSD([sQuery(id+"F0.wireOp",EDGE,"E0.sketch_text.stroke-57"),sQuery(id+"F0.wireOp",EDGE,"E0.sketch_text.stroke-58")])]});
            var Q179;
            Q179=makeQuery(id+"F1.opExtrude","CAP_EDGE",EDGE,{"disambiguationData":[OSD([sQuery(id+"F0.wireOp",EDGE,"E0.sketch_text.stroke-49")])],"isStart":false});
            var Q180;
            Q180=makeQuery(id+"F1.opExtrude","CAP_EDGE",EDGE,{"disambiguationData":[OSD([sQuery(id+"F0.wireOp",EDGE,"E0.sketch_text.stroke-57")])],"isStart":false});
            var Q181;
            Q181=makeQuery(id+"F1.opExtrude","CAP_EDGE",EDGE,{"disambiguationData":[OSD([sQuery(id+"F0.wireOp",EDGE,"E0.sketch_text.stroke-65")])],"isStart":false});
            var Q182;
            Q182=makeQuery(id+"F1.opExtrude","CAP_EDGE",EDGE,{"disambiguationData":[OSD([sQuery(id+"F0.wireOp",EDGE,"E0.sketch_text.stroke-50")])],"isStart":true});
            var Q183;
            Q183=makeQuery(id+"F1.opExtrude","CAP_EDGE",EDGE,{"disambiguationData":[OSD([sQuery(id+"F0.wireOp",EDGE,"E0.sketch_text.stroke-58")])],"isStart":true});
            var Q184;
            Q184=makeQuery(id+"F1.opExtrude","CAP_EDGE",EDGE,{"disambiguationData":[OSD([sQuery(id+"F0.wireOp",EDGE,"E0.sketch_text.stroke-66")])],"isStart":true});
            var Q185;
            Q185=makeQuery(id+"F1.opExtrude","CAP_EDGE",EDGE,{"disambiguationData":[OSD([sQuery(id+"F0.wireOp",EDGE,"E0.sketch_text.stroke-50")])],"isStart":false});
            var Q186;
            Q186=makeQuery(id+"F1.opExtrude","CAP_EDGE",EDGE,{"disambiguationData":[OSD([sQuery(id+"F0.wireOp",EDGE,"E0.sketch_text.stroke-58")])],"isStart":false});
            var Q187;
            Q187=makeQuery(id+"F1.opExtrude","CAP_EDGE",EDGE,{"disambiguationData":[OSD([sQuery(id+"F0.wireOp",EDGE,"E0.sketch_text.stroke-66")])],"isStart":false});
            var Q188;
            Q188=makeQuery(id+"F1.opExtrude","CAP_EDGE",EDGE,{"disambiguationData":[OSD([sQuery(id+"F0.wireOp",EDGE,"E0.sketch_text.stroke-38")])],"isStart":true});
            var Q189;
            Q189=makeQuery(id+"F1.opExtrude","CAP_EDGE",EDGE,{"disambiguationData":[OSD([sQuery(id+"F0.wireOp",EDGE,"E0.sketch_text.stroke-17")])],"isStart":true});
            var Q190;
            Q190=makeQuery(id+"F1.opExtrude","CAP_EDGE",EDGE,{"disambiguationData":[OSD([sQuery(id+"F0.wireOp",EDGE,"E0.sketch_text.stroke-19")])],"isStart":true});
            var Q191;
            Q191=makeQuery(id+"F1.opExtrude","CAP_EDGE",EDGE,{"disambiguationData":[OSD([sQuery(id+"F0.wireOp",EDGE,"E0.sketch_text.stroke-21")])],"isStart":true});
            var Q192;
            Q192=makeQuery(id+"F1.opExtrude","SWEPT_EDGE",EDGE,{"disambiguationData":[OSD([sQuery(id+"F0.wireOp",EDGE,"E0.sketch_text.stroke-19"),sQuery(id+"F0.wireOp",EDGE,"E0.sketch_text.stroke-20")])]});
            var Q193;
            Q193=makeQuery(id+"F1.opExtrude","SWEPT_EDGE",EDGE,{"disambiguationData":[OSD([sQuery(id+"F0.wireOp",EDGE,"E0.sketch_text.stroke-20"),sQuery(id+"F0.wireOp",EDGE,"E0.sketch_text.stroke-21")])]});
            var Q194;
            Q194=makeQuery(id+"F1.opExtrude","CAP_EDGE",EDGE,{"disambiguationData":[OSD([sQuery(id+"F0.wireOp",EDGE,"E0.sketch_text.stroke-23")])],"isStart":false});
            var Q195;
            Q195=makeQuery(id+"F1.opExtrude","SWEPT_EDGE",EDGE,{"disambiguationData":[OSD([sQuery(id+"F0.wireOp",EDGE,"E0.sketch_text.stroke-47"),sQuery(id+"F0.wireOp",EDGE,"E0.sketch_text.stroke-50")])]});
            var Q196;
            Q196=makeQuery(id+"F1.opExtrude","SWEPT_EDGE",EDGE,{"disambiguationData":[OSD([sQuery(id+"F0.wireOp",EDGE,"E0.sketch_text.stroke-47"),sQuery(id+"F0.wireOp",EDGE,"E0.sketch_text.stroke-48")])]});
            var Q197;
            Q197=makeQuery(id+"F1.opExtrude","SWEPT_EDGE",EDGE,{"disambiguationData":[OSD([sQuery(id+"F0.wireOp",EDGE,"E0.sketch_text.stroke-69"),sQuery(id+"F0.wireOp",EDGE,"E0.sketch_text.stroke-70")])]});
            var Q198;
            Q198=makeQuery(id+"F1.opExtrude","SWEPT_EDGE",EDGE,{"disambiguationData":[OSD([sQuery(id+"F0.wireOp",EDGE,"E0.sketch_text.stroke-43"),sQuery(id+"F0.wireOp",EDGE,"E0.sketch_text.stroke-44")])]});
            var Q199;
            Q199=makeQuery(id+"F1.opExtrude","SWEPT_EDGE",EDGE,{"disambiguationData":[OSD([sQuery(id+"F0.wireOp",EDGE,"E0.sketch_text.stroke-23"),sQuery(id+"F0.wireOp",EDGE,"E0.sketch_text.stroke-30")])]});
            var Q200;
            Q200=makeQuery(id+"F1.opExtrude","CAP_EDGE",EDGE,{"disambiguationData":[OSD([sQuery(id+"F0.wireOp",EDGE,"E0.sketch_text.stroke-2")])],"isStart":false});
            var Q201;
            Q201=makeQuery(id+"F1.opExtrude","CAP_EDGE",EDGE,{"disambiguationData":[OSD([sQuery(id+"F0.wireOp",EDGE,"E0.sketch_text.stroke-0")])],"isStart":false});
            var Q202;
            Q202=makeQuery(id+"F1.opExtrude","SWEPT_EDGE",EDGE,{"disambiguationData":[OSD([sQuery(id+"F0.wireOp",EDGE,"E0.sketch_text.stroke-59"),sQuery(id+"F0.wireOp",EDGE,"E0.sketch_text.stroke-60")])]});
            var Q203;
            Q203=makeQuery(id+"F1.opExtrude","SWEPT_FACE",FACE,{"disambiguationData":[OSD([sQuery(id+"F0.wireOp",EDGE,"E0.sketch_text.stroke-0")])]});
            var Q204;
            Q204=makeQuery(id+"F1.opExtrude","CAP_EDGE",EDGE,{"disambiguationData":[OSD([sQuery(id+"F0.wireOp",EDGE,"E0.sketch_text.stroke-59")])],"isStart":false});
            var Q205;
            Q205=makeQuery(id+"F1.opExtrude","SWEPT_EDGE",EDGE,{"disambiguationData":[OSD([sQuery(id+"F0.wireOp",EDGE,"E0.sketch_text.stroke-60"),sQuery(id+"F0.wireOp",EDGE,"E0.sketch_text.stroke-61")])]});
            var Q206;
            Q206=makeQuery(id+"F1.opExtrude","CAP_EDGE",EDGE,{"disambiguationData":[OSD([sQuery(id+"F0.wireOp",EDGE,"E0.sketch_text.stroke-60")])],"isStart":false});
            var Q207;
            Q207=makeQuery(id+"F1.opExtrude","CAP_EDGE",EDGE,{"disambiguationData":[OSD([sQuery(id+"F0.wireOp",EDGE,"E0.sketch_text.stroke-61")])],"isStart":false});
            var Q208;
            Q208=makeQuery(id+"F1.opExtrude","SWEPT_EDGE",EDGE,{"disambiguationData":[OSD([sQuery(id+"F0.wireOp",EDGE,"E0.sketch_text.stroke-31"),sQuery(id+"F0.wireOp",EDGE,"E0.sketch_text.stroke-32")])]});
            var Q209;
            Q209=makeQuery(id+"F1.opExtrude","CAP_EDGE",EDGE,{"disambiguationData":[OSD([sQuery(id+"F0.wireOp",EDGE,"E0.sketch_text.stroke-31")])],"isStart":false});
            var Q210;
            Q210=makeQuery(id+"F1.opExtrude","CAP_EDGE",EDGE,{"disambiguationData":[OSD([sQuery(id+"F0.wireOp",EDGE,"E0.sketch_text.stroke-32")])],"isStart":false});
            var Q211;
            Q211=makeQuery(id+"F1.opExtrude","SWEPT_EDGE",EDGE,{"disambiguationData":[OSD([sQuery(id+"F0.wireOp",EDGE,"E0.sketch_text.stroke-0"),sQuery(id+"F0.wireOp",EDGE,"E0.sketch_text.stroke-1")])]});
            var Q212;
            Q212=makeQuery(id+"F1.opExtrude","SWEPT_EDGE",EDGE,{"disambiguationData":[OSD([sQuery(id+"F0.wireOp",EDGE,"E0.sketch_text.stroke-1"),sQuery(id+"F0.wireOp",EDGE,"E0.sketch_text.stroke-2")])]});
            var Q213;
            Q213=makeQuery(id+"F1.opExtrude","CAP_EDGE",EDGE,{"disambiguationData":[OSD([sQuery(id+"F0.wireOp",EDGE,"E0.sketch_text.stroke-1")])],"isStart":false});
            fillet(context, id + "F2", {"entities" : qUnion([Q0, Q1, Q2, Q3, Q4, Q5, Q6, Q7, Q8, Q9, Q10, Q11, Q12, Q13, Q14, Q15, Q16, Q17, Q18, Q19, Q20, Q21, Q22, Q23, Q24, Q25, Q26, Q27, Q28, Q29, Q30, Q31, Q32, Q33, Q34, Q35, Q36, Q37, Q38, Q39, Q40, Q41, Q42, Q43, Q44, Q45, Q46, Q47, Q48, Q49, Q50, Q51, Q52, Q53, Q54, Q55, Q56, Q57, Q58, Q59, Q60, Q61, Q62, Q63, Q64, Q65, Q66, Q67, Q68, Q69, Q70, Q71, Q72, Q73, Q74, Q75, Q76, Q77, Q78, Q79, Q80, Q81, Q82, Q83, Q84, Q85, Q86, Q87, Q88, Q89, Q90, Q91, Q92, Q93, Q94, Q95, Q96, Q97, Q98, Q99, Q100, Q101, Q102, Q103, Q104, Q105, Q106, Q107, Q108, Q109, Q110, Q111, Q112, Q113, Q114, Q115, Q116, Q117, Q118, Q119, Q120, Q121, Q122, Q123, Q124, Q125, Q126, Q127, Q128, Q129, Q130, Q131, Q132, Q133, Q134, Q135, Q136, Q137, Q138, Q139, Q140, Q141, Q142, Q143, Q144, Q145, Q146, Q147, Q148, Q149, Q150, Q151, Q152, Q153, Q154, Q155, Q156, Q157, Q158, Q159, Q160, Q161, Q162, Q163, Q164, Q165, Q166, Q167, Q168, Q169, Q170, Q171, Q172, Q173, Q174, Q175, Q176, Q177, Q178, Q179, Q180, Q181, Q182, Q183, Q184, Q185, Q186, Q187, Q188, Q189, Q190, Q191, Q192, Q193, Q194, Q195, Q196, Q197, Q198, Q199, Q200, Q201, Q202, Q203, Q204, Q205, Q206, Q207, Q208, Q209, Q210, Q211, Q212, Q213]), "radius" : 1 * mm, "tangentPropagation" : true, "allowEdgeOverflow" : false});
        }
        {
            var Q0;
            Q0=makeQuery(id+"F1.opExtrude","CAP_FACE",FACE,{"disambiguationData":[OSD([sQuery(id+"F0.wireOp",EDGE,"E0.sketch_text.stroke-0"),sQuery(id+"F0.wireOp",EDGE,"E0.sketch_text.stroke-1"),sQuery(id+"F0.wireOp",EDGE,"E0.sketch_text.stroke-2"),sQuery(id+"F0.wireOp",EDGE,"E0.sketch_text.stroke-3"),sQuery(id+"F0.wireOp",EDGE,"E0.sketch_text.stroke-4"),sQuery(id+"F0.wireOp",EDGE,"E0.sketch_text.stroke-5"),sQuery(id+"F0.wireOp",EDGE,"E0.sketch_text.stroke-6"),sQuery(id+"F0.wireOp",EDGE,"E0.sketch_text.stroke-7"),sQuery(id+"F0.wireOp",EDGE,"E0.sketch_text.stroke-8"),sQuery(id+"F0.wireOp",EDGE,"E0.sketch_text.stroke-9"),sQuery(id+"F0.wireOp",EDGE,"E0.sketch_text.stroke-10"),sQuery(id+"F0.wireOp",EDGE,"E0.sketch_text.stroke-11"),sQuery(id+"F0.wireOp",EDGE,"E0.sketch_text.stroke-12"),sQuery(id+"F0.wireOp",EDGE,"E0.sketch_text.stroke-13"),sQuery(id+"F0.wireOp",EDGE,"E0.sketch_text.stroke-14"),sQuery(id+"F0.wireOp",EDGE,"E0.sketch_text.stroke-15"),sQuery(id+"F0.wireOp",EDGE,"E0.sketch_text.stroke-16"),sQuery(id+"F0.wireOp",EDGE,"E0.sketch_text.stroke-17"),sQuery(id+"F0.wireOp",EDGE,"E0.sketch_text.stroke-18")])],"isStart":false});
            cPlane(context, id + "F3", {"entities" : qUnion([Q0]), "cplaneType" : CPlaneType.OFFSET, "offset" : 20 * mm, "oppositeDirection" : true, "width" : 152.4 * mm, "height" : 152.4 * mm});
        }
        {
            var Q0;
            Q0=qCreatedBy(id+"F3.planeOp",FACE);
            var sketch = newSketch(context, id + "F4", { "sketchPlane" : qUnion([Q0])});
            skLineSegment(sketch, "E1.bottom", {"start": v(-88.26, 33.6) * mm, "end": v(76.87, 33.6) * mm});
            skLineSegment(sketch, "E1.top", {"start": v(-88.26, -28.92) * mm, "end": v(76.87, -28.92) * mm});
            skLineSegment(sketch, "E1.left", {"start": v(-88.26, 33.6) * mm, "end": v(-88.26, -28.92) * mm});
            skLineSegment(sketch, "E1.right", {"start": v(76.87, 33.6) * mm, "end": v(76.87, -28.92) * mm});
            skSolve(sketch);
        }
        {
            var Q0;
            Q0=makeQuery(id+"F4.imprint","IMPRINT",FACE,{"disambiguationData":[TD([[makeQuery(id+"F4.imprint","IMPRINT",EDGE,{"derivedFrom":sQuery(id+"F4.wireOp",EDGE,"E1.bottom")}),-1.0]])]});
            extrude(context, id + "F5", {"entities" : qUnion([Q0]), "oppositeDirection" : true, "depth" : 2 * mm, "offsetDistance" : 25.4 * mm});
        }
        {
            var Q0;
            Q0=makeQuery(id+"F5.opExtrude","SWEPT_EDGE",EDGE,{"disambiguationData":[OSD([sQuery(id+"F4.wireOp",EDGE,"E1.top"),sQuery(id+"F4.wireOp",EDGE,"E1.left")])]});
            var Q1;
            Q1=makeQuery(id+"F5.opExtrude","SWEPT_EDGE",EDGE,{"disambiguationData":[OSD([sQuery(id+"F4.wireOp",EDGE,"E1.bottom"),sQuery(id+"F4.wireOp",EDGE,"E1.left")])]});
            var Q2;
            Q2=makeQuery(id+"F5.opExtrude","SWEPT_EDGE",EDGE,{"disambiguationData":[OSD([sQuery(id+"F4.wireOp",EDGE,"E1.bottom"),sQuery(id+"F4.wireOp",EDGE,"E1.right")])]});
            var Q3;
            Q3=makeQuery(id+"F5.opExtrude","SWEPT_EDGE",EDGE,{"disambiguationData":[OSD([sQuery(id+"F4.wireOp",EDGE,"E1.top"),sQuery(id+"F4.wireOp",EDGE,"E1.right")])]});
            fillet(context, id + "F6", {"entities" : qUnion([Q0, Q1, Q2, Q3]), "radius" : 7.62 * mm, "tangentPropagation" : true, "allowEdgeOverflow" : false});
        }
        {
            var Q0;
            Q0=makeQuery(id+"F5.opExtrude","CAP_FACE",FACE,{"disambiguationData":[OSD([sQuery(id+"F4.wireOp",EDGE,"E1.bottom"),sQuery(id+"F4.wireOp",EDGE,"E1.top"),sQuery(id+"F4.wireOp",EDGE,"E1.left"),sQuery(id+"F4.wireOp",EDGE,"E1.right")])],"isStart":false});
            var sketch = newSketch(context, id + "F7", { "sketchPlane" : qUnion([Q0])});
            skText(sketch, "E2", { "text": "指考", "fontName": "NotoSansCJKtc-Bold.otf"});
            const initialGuessF7  = {"E2": [-0.06475, -0.0249, 1, 0, 0.045]};
            skSetInitialGuess(sketch, initialGuessF7);
            skSolve(sketch);
        }
        {
            var Q0;
            Q0 = qSketchRegion(id + "F7", true);
            extrude(context, id + "F8", {"entities" : qUnion([Q0]), "operationType" : NewBodyOperationType.ADD, "depth" : 20 * mm, "offsetDistance" : 25.4 * mm});
        }
        {
            var Q0;
            Q0=makeQuery(id+"F8.opExtrude","CAP_FACE",FACE,{"disambiguationData":[OSD([sQuery(id+"F7.wireOp",EDGE,"E2.sketch_text.stroke-0"),sQuery(id+"F7.wireOp",EDGE,"E2.sketch_text.stroke-1"),sQuery(id+"F7.wireOp",EDGE,"E2.sketch_text.stroke-2"),sQuery(id+"F7.wireOp",EDGE,"E2.sketch_text.stroke-3"),sQuery(id+"F7.wireOp",EDGE,"E2.sketch_text.stroke-4"),sQuery(id+"F7.wireOp",EDGE,"E2.sketch_text.stroke-5"),sQuery(id+"F7.wireOp",EDGE,"E2.sketch_text.stroke-6"),sQuery(id+"F7.wireOp",EDGE,"E2.sketch_text.stroke-7"),sQuery(id+"F7.wireOp",EDGE,"E2.sketch_text.stroke-8"),sQuery(id+"F7.wireOp",EDGE,"E2.sketch_text.stroke-9"),sQuery(id+"F7.wireOp",EDGE,"E2.sketch_text.stroke-10"),sQuery(id+"F7.wireOp",EDGE,"E2.sketch_text.stroke-11"),sQuery(id+"F7.wireOp",EDGE,"E2.sketch_text.stroke-12"),sQuery(id+"F7.wireOp",EDGE,"E2.sketch_text.stroke-13"),sQuery(id+"F7.wireOp",EDGE,"E2.sketch_text.stroke-14"),sQuery(id+"F7.wireOp",EDGE,"E2.sketch_text.stroke-15"),sQuery(id+"F7.wireOp",EDGE,"E2.sketch_text.stroke-16"),sQuery(id+"F7.wireOp",EDGE,"E2.sketch_text.stroke-17"),sQuery(id+"F7.wireOp",EDGE,"E2.sketch_text.stroke-18"),sQuery(id+"F7.wireOp",EDGE,"E2.sketch_text.stroke-19"),sQuery(id+"F7.wireOp",EDGE,"E2.sketch_text.stroke-20"),sQuery(id+"F7.wireOp",EDGE,"E2.sketch_text.stroke-21"),sQuery(id+"F7.wireOp",EDGE,"E2.sketch_text.stroke-22"),sQuery(id+"F7.wireOp",EDGE,"E2.sketch_text.stroke-23")])],"isStart":false});
            var Q1;
            Q1=makeQuery(id+"F8.opExtrude","CAP_FACE",FACE,{"disambiguationData":[OSD([sQuery(id+"F7.wireOp",EDGE,"E2.sketch_text.stroke-24"),sQuery(id+"F7.wireOp",EDGE,"E2.sketch_text.stroke-25"),sQuery(id+"F7.wireOp",EDGE,"E2.sketch_text.stroke-26"),sQuery(id+"F7.wireOp",EDGE,"E2.sketch_text.stroke-27"),sQuery(id+"F7.wireOp",EDGE,"E2.sketch_text.stroke-28"),sQuery(id+"F7.wireOp",EDGE,"E2.sketch_text.stroke-29"),sQuery(id+"F7.wireOp",EDGE,"E2.sketch_text.stroke-30"),sQuery(id+"F7.wireOp",EDGE,"E2.sketch_text.stroke-31"),sQuery(id+"F7.wireOp",EDGE,"E2.sketch_text.stroke-32"),sQuery(id+"F7.wireOp",EDGE,"E2.sketch_text.stroke-33"),sQuery(id+"F7.wireOp",EDGE,"E2.sketch_text.stroke-34"),sQuery(id+"F7.wireOp",EDGE,"E2.sketch_text.stroke-35"),sQuery(id+"F7.wireOp",EDGE,"E2.sketch_text.stroke-36"),sQuery(id+"F7.wireOp",EDGE,"E2.sketch_text.stroke-37")])],"isStart":false});
            var Q2;
            Q2=makeQuery(id+"F8.opExtrude","CAP_FACE",FACE,{"disambiguationData":[OSD([sQuery(id+"F7.wireOp",EDGE,"E2.sketch_text.stroke-38"),sQuery(id+"F7.wireOp",EDGE,"E2.sketch_text.stroke-39"),sQuery(id+"F7.wireOp",EDGE,"E2.sketch_text.stroke-40"),sQuery(id+"F7.wireOp",EDGE,"E2.sketch_text.stroke-41"),sQuery(id+"F7.wireOp",EDGE,"E2.sketch_text.stroke-42"),sQuery(id+"F7.wireOp",EDGE,"E2.sketch_text.stroke-43"),sQuery(id+"F7.wireOp",EDGE,"E2.sketch_text.stroke-44"),sQuery(id+"F7.wireOp",EDGE,"E2.sketch_text.stroke-45"),sQuery(id+"F7.wireOp",EDGE,"E2.sketch_text.stroke-46"),sQuery(id+"F7.wireOp",EDGE,"E2.sketch_text.stroke-47"),sQuery(id+"F7.wireOp",EDGE,"E2.sketch_text.stroke-48"),sQuery(id+"F7.wireOp",EDGE,"E2.sketch_text.stroke-49"),sQuery(id+"F7.wireOp",EDGE,"E2.sketch_text.stroke-50"),sQuery(id+"F7.wireOp",EDGE,"E2.sketch_text.stroke-51"),sQuery(id+"F7.wireOp",EDGE,"E2.sketch_text.stroke-52"),sQuery(id+"F7.wireOp",EDGE,"E2.sketch_text.stroke-53")])],"isStart":false});
            var Q3;
            Q3=makeQuery(id+"F8.opExtrude","CAP_FACE",FACE,{"disambiguationData":[OSD([sQuery(id+"F7.wireOp",EDGE,"E2.sketch_text.stroke-54"),sQuery(id+"F7.wireOp",EDGE,"E2.sketch_text.stroke-55"),sQuery(id+"F7.wireOp",EDGE,"E2.sketch_text.stroke-56"),sQuery(id+"F7.wireOp",EDGE,"E2.sketch_text.stroke-57"),sQuery(id+"F7.wireOp",EDGE,"E2.sketch_text.stroke-58"),sQuery(id+"F7.wireOp",EDGE,"E2.sketch_text.stroke-59"),sQuery(id+"F7.wireOp",EDGE,"E2.sketch_text.stroke-60"),sQuery(id+"F7.wireOp",EDGE,"E2.sketch_text.stroke-61"),sQuery(id+"F7.wireOp",EDGE,"E2.sketch_text.stroke-62"),sQuery(id+"F7.wireOp",EDGE,"E2.sketch_text.stroke-63"),sQuery(id+"F7.wireOp",EDGE,"E2.sketch_text.stroke-64"),sQuery(id+"F7.wireOp",EDGE,"E2.sketch_text.stroke-65"),sQuery(id+"F7.wireOp",EDGE,"E2.sketch_text.stroke-66"),sQuery(id+"F7.wireOp",EDGE,"E2.sketch_text.stroke-67"),sQuery(id+"F7.wireOp",EDGE,"E2.sketch_text.stroke-68"),sQuery(id+"F7.wireOp",EDGE,"E2.sketch_text.stroke-69"),sQuery(id+"F7.wireOp",EDGE,"E2.sketch_text.stroke-70"),sQuery(id+"F7.wireOp",EDGE,"E2.sketch_text.stroke-71"),sQuery(id+"F7.wireOp",EDGE,"E2.sketch_text.stroke-72"),sQuery(id+"F7.wireOp",EDGE,"E2.sketch_text.stroke-73"),sQuery(id+"F7.wireOp",EDGE,"E2.sketch_text.stroke-74"),sQuery(id+"F7.wireOp",EDGE,"E2.sketch_text.stroke-75"),sQuery(id+"F7.wireOp",EDGE,"E2.sketch_text.stroke-76"),sQuery(id+"F7.wireOp",EDGE,"E2.sketch_text.stroke-77"),sQuery(id+"F7.wireOp",EDGE,"E2.sketch_text.stroke-78"),sQuery(id+"F7.wireOp",EDGE,"E2.sketch_text.stroke-79"),sQuery(id+"F7.wireOp",EDGE,"E2.sketch_text.stroke-80"),sQuery(id+"F7.wireOp",EDGE,"E2.sketch_text.stroke-81"),sQuery(id+"F7.wireOp",EDGE,"E2.sketch_text.stroke-82"),sQuery(id+"F7.wireOp",EDGE,"E2.sketch_text.stroke-83"),sQuery(id+"F7.wireOp",EDGE,"E2.sketch_text.stroke-84"),sQuery(id+"F7.wireOp",EDGE,"E2.sketch_text.stroke-85"),sQuery(id+"F7.wireOp",EDGE,"E2.sketch_text.stroke-86"),sQuery(id+"F7.wireOp",EDGE,"E2.sketch_text.stroke-87"),sQuery(id+"F7.wireOp",EDGE,"E2.sketch_text.stroke-88"),sQuery(id+"F7.wireOp",EDGE,"E2.sketch_text.stroke-89"),sQuery(id+"F7.wireOp",EDGE,"E2.sketch_text.stroke-90"),sQuery(id+"F7.wireOp",EDGE,"E2.sketch_text.stroke-91"),sQuery(id+"F7.wireOp",EDGE,"E2.sketch_text.stroke-92"),sQuery(id+"F7.wireOp",EDGE,"E2.sketch_text.stroke-93"),sQuery(id+"F7.wireOp",EDGE,"E2.sketch_text.stroke-94")])],"isStart":false});
            var Q4;
            Q4=makeQuery(id+"F8.opExtrude","SWEPT_EDGE",EDGE,{"disambiguationData":[OSD([sQuery(id+"F7.wireOp",EDGE,"E2.sketch_text.stroke-51"),sQuery(id+"F7.wireOp",EDGE,"E2.sketch_text.stroke-52")])]});
            var Q5;
            Q5=makeQuery(id+"F8.opExtrude","SWEPT_EDGE",EDGE,{"disambiguationData":[OSD([sQuery(id+"F7.wireOp",EDGE,"E2.sketch_text.stroke-25"),sQuery(id+"F7.wireOp",EDGE,"E2.sketch_text.stroke-26")])]});
            var Q6;
            Q6=makeQuery(id+"F8.opExtrude","SWEPT_EDGE",EDGE,{"disambiguationData":[OSD([sQuery(id+"F7.wireOp",EDGE,"E2.sketch_text.stroke-49"),sQuery(id+"F7.wireOp",EDGE,"E2.sketch_text.stroke-50")])]});
            var Q7;
            Q7=makeQuery(id+"F8.opExtrude","SWEPT_EDGE",EDGE,{"disambiguationData":[OSD([sQuery(id+"F7.wireOp",EDGE,"E2.sketch_text.stroke-50"),sQuery(id+"F7.wireOp",EDGE,"E2.sketch_text.stroke-51")])]});
            var Q8;
            Q8=makeQuery(id+"F8.opExtrude","SWEPT_EDGE",EDGE,{"disambiguationData":[OSD([sQuery(id+"F7.wireOp",EDGE,"E2.sketch_text.stroke-46"),sQuery(id+"F7.wireOp",EDGE,"E2.sketch_text.stroke-47")])]});
            var Q9;
            Q9=makeQuery(id+"F8.opExtrude","SWEPT_EDGE",EDGE,{"disambiguationData":[OSD([sQuery(id+"F7.wireOp",EDGE,"E2.sketch_text.stroke-46"),sQuery(id+"F7.wireOp",EDGE,"E2.sketch_text.stroke-53")])]});
            var Q10;
            Q10=makeQuery(id+"F8.opExtrude","SWEPT_EDGE",EDGE,{"disambiguationData":[OSD([sQuery(id+"F7.wireOp",EDGE,"E2.sketch_text.stroke-13"),sQuery(id+"F7.wireOp",EDGE,"E2.sketch_text.stroke-14")])]});
            var Q11;
            Q11=makeQuery(id+"F8.opExtrude","SWEPT_EDGE",EDGE,{"disambiguationData":[OSD([sQuery(id+"F7.wireOp",EDGE,"E2.sketch_text.stroke-12"),sQuery(id+"F7.wireOp",EDGE,"E2.sketch_text.stroke-13")])]});
            var Q12;
            Q12=makeQuery(id+"F8.opExtrude","SWEPT_EDGE",EDGE,{"disambiguationData":[OSD([sQuery(id+"F7.wireOp",EDGE,"E2.sketch_text.stroke-22"),sQuery(id+"F7.wireOp",EDGE,"E2.sketch_text.stroke-23")])]});
            var Q13;
            Q13=makeQuery(id+"F8.opExtrude","SWEPT_EDGE",EDGE,{"disambiguationData":[OSD([sQuery(id+"F7.wireOp",EDGE,"E2.sketch_text.stroke-2"),sQuery(id+"F7.wireOp",EDGE,"E2.sketch_text.stroke-3")])]});
            var Q14;
            Q14=makeQuery(id+"F8.opExtrude","SWEPT_EDGE",EDGE,{"disambiguationData":[OSD([sQuery(id+"F7.wireOp",EDGE,"E2.sketch_text.stroke-9"),sQuery(id+"F7.wireOp",EDGE,"E2.sketch_text.stroke-10")])]});
            var Q15;
            Q15=makeQuery(id+"F8.opExtrude","SWEPT_EDGE",EDGE,{"disambiguationData":[OSD([sQuery(id+"F7.wireOp",EDGE,"E2.sketch_text.stroke-8"),sQuery(id+"F7.wireOp",EDGE,"E2.sketch_text.stroke-9")])]});
            var Q16;
            Q16=makeQuery(id+"F8.opExtrude","SWEPT_EDGE",EDGE,{"disambiguationData":[OSD([sQuery(id+"F7.wireOp",EDGE,"E2.sketch_text.stroke-17"),sQuery(id+"F7.wireOp",EDGE,"E2.sketch_text.stroke-18")])]});
            var Q17;
            Q17=makeQuery(id+"F8.opExtrude","SWEPT_EDGE",EDGE,{"disambiguationData":[OSD([sQuery(id+"F7.wireOp",EDGE,"E2.sketch_text.stroke-82"),sQuery(id+"F7.wireOp",EDGE,"E2.sketch_text.stroke-83")])]});
            var Q18;
            Q18=makeQuery(id+"F8.opExtrude","SWEPT_EDGE",EDGE,{"disambiguationData":[OSD([sQuery(id+"F7.wireOp",EDGE,"E2.sketch_text.stroke-83"),sQuery(id+"F7.wireOp",EDGE,"E2.sketch_text.stroke-84")])]});
            var Q19;
            Q19=makeQuery(id+"F8.opExtrude","SWEPT_EDGE",EDGE,{"disambiguationData":[OSD([sQuery(id+"F7.wireOp",EDGE,"E2.sketch_text.stroke-78"),sQuery(id+"F7.wireOp",EDGE,"E2.sketch_text.stroke-79")])]});
            var Q20;
            Q20=makeQuery(id+"F8.opExtrude","SWEPT_EDGE",EDGE,{"disambiguationData":[OSD([sQuery(id+"F7.wireOp",EDGE,"E2.sketch_text.stroke-76"),sQuery(id+"F7.wireOp",EDGE,"E2.sketch_text.stroke-77")])]});
            var Q21;
            Q21=makeQuery(id+"F8.opExtrude","SWEPT_EDGE",EDGE,{"disambiguationData":[OSD([sQuery(id+"F7.wireOp",EDGE,"E2.sketch_text.stroke-75"),sQuery(id+"F7.wireOp",EDGE,"E2.sketch_text.stroke-76")])]});
            var Q22;
            Q22=makeQuery(id+"F8.opExtrude","SWEPT_EDGE",EDGE,{"disambiguationData":[OSD([sQuery(id+"F7.wireOp",EDGE,"E2.sketch_text.stroke-6"),sQuery(id+"F7.wireOp",EDGE,"E2.sketch_text.stroke-7")])]});
            var Q23;
            Q23=makeQuery(id+"F8.opExtrude","SWEPT_EDGE",EDGE,{"disambiguationData":[OSD([sQuery(id+"F7.wireOp",EDGE,"E2.sketch_text.stroke-68"),sQuery(id+"F7.wireOp",EDGE,"E2.sketch_text.stroke-69")])]});
            var Q24;
            Q24=makeQuery(id+"F8.opExtrude","SWEPT_EDGE",EDGE,{"disambiguationData":[OSD([sQuery(id+"F7.wireOp",EDGE,"E2.sketch_text.stroke-69"),sQuery(id+"F7.wireOp",EDGE,"E2.sketch_text.stroke-70")])]});
            var Q25;
            Q25=makeQuery(id+"F8.opExtrude","SWEPT_EDGE",EDGE,{"disambiguationData":[OSD([sQuery(id+"F7.wireOp",EDGE,"E2.sketch_text.stroke-66"),sQuery(id+"F7.wireOp",EDGE,"E2.sketch_text.stroke-67")])]});
            var Q26;
            Q26=makeQuery(id+"F8.opExtrude","SWEPT_EDGE",EDGE,{"disambiguationData":[OSD([sQuery(id+"F7.wireOp",EDGE,"E2.sketch_text.stroke-73"),sQuery(id+"F7.wireOp",EDGE,"E2.sketch_text.stroke-74")])]});
            var Q27;
            Q27=makeQuery(id+"F8.opExtrude","SWEPT_EDGE",EDGE,{"disambiguationData":[OSD([sQuery(id+"F7.wireOp",EDGE,"E2.sketch_text.stroke-72"),sQuery(id+"F7.wireOp",EDGE,"E2.sketch_text.stroke-73")])]});
            var Q28;
            Q28=makeQuery(id+"F8.opExtrude","SWEPT_EDGE",EDGE,{"disambiguationData":[OSD([sQuery(id+"F7.wireOp",EDGE,"E2.sketch_text.stroke-34"),sQuery(id+"F7.wireOp",EDGE,"E2.sketch_text.stroke-35")])]});
            var Q29;
            Q29=makeQuery(id+"F8.opExtrude","SWEPT_EDGE",EDGE,{"disambiguationData":[OSD([sQuery(id+"F7.wireOp",EDGE,"E2.sketch_text.stroke-33"),sQuery(id+"F7.wireOp",EDGE,"E2.sketch_text.stroke-34")])]});
            var Q30;
            Q30=makeQuery(id+"F8.opExtrude","SWEPT_EDGE",EDGE,{"disambiguationData":[OSD([sQuery(id+"F7.wireOp",EDGE,"E2.sketch_text.stroke-31"),sQuery(id+"F7.wireOp",EDGE,"E2.sketch_text.stroke-32")])]});
            var Q31;
            Q31=makeQuery(id+"F8.opExtrude","SWEPT_EDGE",EDGE,{"disambiguationData":[OSD([sQuery(id+"F7.wireOp",EDGE,"E2.sketch_text.stroke-65"),sQuery(id+"F7.wireOp",EDGE,"E2.sketch_text.stroke-66")])]});
            var Q32;
            Q32=makeQuery(id+"F8.opExtrude","SWEPT_EDGE",EDGE,{"disambiguationData":[OSD([sQuery(id+"F7.wireOp",EDGE,"E2.sketch_text.stroke-63"),sQuery(id+"F7.wireOp",EDGE,"E2.sketch_text.stroke-64")])]});
            var Q33;
            Q33=makeQuery(id+"F8.opExtrude","SWEPT_EDGE",EDGE,{"disambiguationData":[OSD([sQuery(id+"F7.wireOp",EDGE,"E2.sketch_text.stroke-60"),sQuery(id+"F7.wireOp",EDGE,"E2.sketch_text.stroke-61")])]});
            var Q34;
            Q34=makeQuery(id+"F8.opExtrude","SWEPT_EDGE",EDGE,{"disambiguationData":[OSD([sQuery(id+"F7.wireOp",EDGE,"E2.sketch_text.stroke-61"),sQuery(id+"F7.wireOp",EDGE,"E2.sketch_text.stroke-62")])]});
            var Q35;
            Q35=makeQuery(id+"F8.opExtrude","SWEPT_EDGE",EDGE,{"disambiguationData":[OSD([sQuery(id+"F7.wireOp",EDGE,"E2.sketch_text.stroke-58"),sQuery(id+"F7.wireOp",EDGE,"E2.sketch_text.stroke-59")])]});
            var Q36;
            Q36=makeQuery(id+"F8.opExtrude","SWEPT_EDGE",EDGE,{"disambiguationData":[OSD([sQuery(id+"F7.wireOp",EDGE,"E2.sketch_text.stroke-58"),sQuery(id+"F7.wireOp",EDGE,"E2.sketch_text.stroke-94")])]});
            var Q37;
            Q37=makeQuery(id+"F8.opExtrude","SWEPT_EDGE",EDGE,{"disambiguationData":[OSD([sQuery(id+"F7.wireOp",EDGE,"E2.sketch_text.stroke-91"),sQuery(id+"F7.wireOp",EDGE,"E2.sketch_text.stroke-92")])]});
            var Q38;
            Q38=makeQuery(id+"F8.opExtrude","SWEPT_EDGE",EDGE,{"disambiguationData":[OSD([sQuery(id+"F7.wireOp",EDGE,"E2.sketch_text.stroke-90"),sQuery(id+"F7.wireOp",EDGE,"E2.sketch_text.stroke-91")])]});
            var Q39;
            Q39=makeQuery(id+"F8.opExtrude","SWEPT_EDGE",EDGE,{"disambiguationData":[OSD([sQuery(id+"F7.wireOp",EDGE,"E2.sketch_text.stroke-87"),sQuery(id+"F7.wireOp",EDGE,"E2.sketch_text.stroke-88")])]});
            var Q40;
            Q40=makeQuery(id+"F8.opExtrude","SWEPT_EDGE",EDGE,{"disambiguationData":[OSD([sQuery(id+"F7.wireOp",EDGE,"E2.sketch_text.stroke-0"),sQuery(id+"F7.wireOp",EDGE,"E2.sketch_text.stroke-23")])]});
            var Q41;
            Q41=makeQuery(id+"F8.opExtrude","SWEPT_EDGE",EDGE,{"disambiguationData":[OSD([sQuery(id+"F7.wireOp",EDGE,"E2.sketch_text.stroke-3"),sQuery(id+"F7.wireOp",EDGE,"E2.sketch_text.stroke-4")])]});
            var Q42;
            Q42=makeQuery(id+"F8.opExtrude","SWEPT_EDGE",EDGE,{"disambiguationData":[OSD([sQuery(id+"F7.wireOp",EDGE,"E2.sketch_text.stroke-30"),sQuery(id+"F7.wireOp",EDGE,"E2.sketch_text.stroke-31")])]});
            var Q43;
            Q43=makeQuery(id+"F8.opExtrude","SWEPT_EDGE",EDGE,{"disambiguationData":[OSD([sQuery(id+"F7.wireOp",EDGE,"E2.sketch_text.stroke-24"),sQuery(id+"F7.wireOp",EDGE,"E2.sketch_text.stroke-25")])]});
            var Q44;
            Q44=makeQuery(id+"F8.opExtrude","CAP_EDGE",EDGE,{"disambiguationData":[OSD([sQuery(id+"F7.wireOp",EDGE,"E2.sketch_text.stroke-63")])],"isStart":false});
            fillet(context, id + "F9", {"entities" : qUnion([Q0, Q1, Q2, Q3, Q4, Q5, Q6, Q7, Q8, Q9, Q10, Q11, Q12, Q13, Q14, Q15, Q16, Q17, Q18, Q19, Q20, Q21, Q22, Q23, Q24, Q25, Q26, Q27, Q28, Q29, Q30, Q31, Q32, Q33, Q34, Q35, Q36, Q37, Q38, Q39, Q40, Q41, Q42, Q43, Q44]), "radius" : 2 * mm, "tangentPropagation" : true, "allowEdgeOverflow" : false});
        }
        {
            var Q0;
            Q0=makeQuery(id+"F5.opExtrude","CAP_FACE",FACE,{"disambiguationData":[OSD([sQuery(id+"F4.wireOp",EDGE,"E1.bottom"),sQuery(id+"F4.wireOp",EDGE,"E1.top"),sQuery(id+"F4.wireOp",EDGE,"E1.left"),sQuery(id+"F4.wireOp",EDGE,"E1.right")])],"isStart":true});
            var sketch = newSketch(context, id + "F10", { "sketchPlane" : qUnion([Q0])});
            skPoint(sketch, "E3", {"position": v(-80.02, 21.87) * mm});
            skSolve(sketch);
        }
        {
            var Q0;
            Q0=sQuery(id+"F10.wireOp",VERTEX,"E3");
            var Q1;
            Q1=makeQuery(id+"F5.opExtrude","SWEPT_BODY",BODY,{"disambiguationData":[OSD([sQuery(id+"F4.wireOp",EDGE,"E1.bottom"),sQuery(id+"F4.wireOp",EDGE,"E1.top"),sQuery(id+"F4.wireOp",EDGE,"E1.left"),sQuery(id+"F4.wireOp",EDGE,"E1.right")])]});
            hole(context, id + "F11", {"style" : HoleStyle.SIMPLE, "endStyle" : HoleEndStyle.THROUGH, "holeDiameter" : 3.5 * mm, "majorDiameter" : 6.35 * mm, "isTappedThrough" : true, "tappedDepth" : 12.7 * mm, "tapClearance" : 3, "locations" : qUnion([Q0]), "scope" : qUnion([Q1])});
        }
    });
